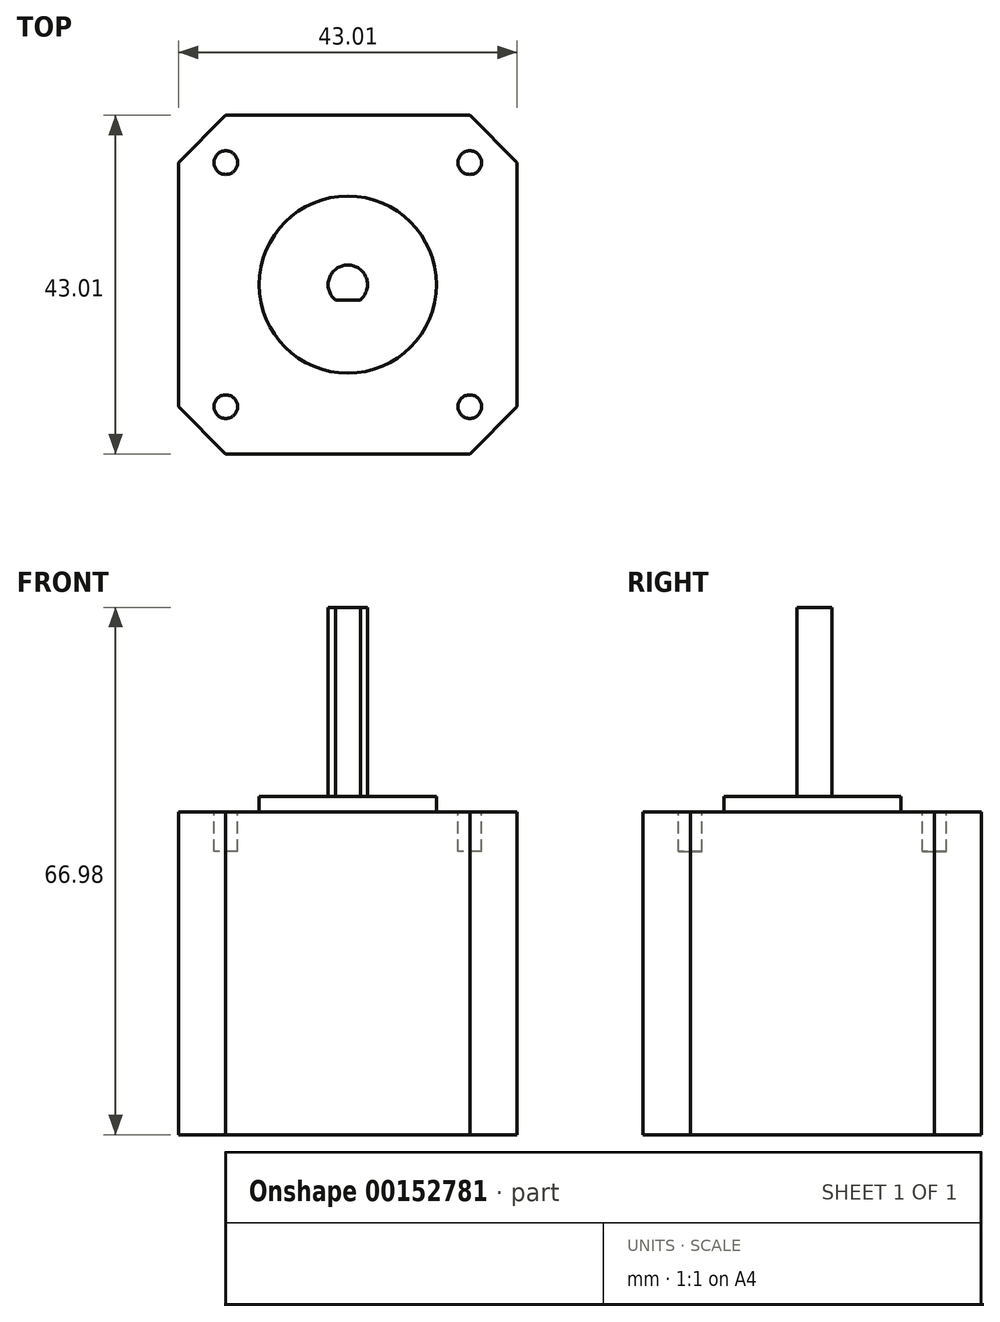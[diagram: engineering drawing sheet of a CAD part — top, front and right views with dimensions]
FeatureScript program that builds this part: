
annotation { "Feature Type Name" : "Feature", "Feature Type Description" : "" }
export const myFeature = defineFeature(function(context is Context, id is Id, definition is map)
    precondition{}
    {
        {
            var Q0;
            Q0=qCreatedBy(makeId("Top.planeOp"),FACE);
            var sketch = newSketch(context, id + "F0", { "sketchPlane" : qUnion([Q0])});
            skLineSegment(sketch, "E0.bottom", {"start": v(0, 0) * mm, "end": v(43, 0) * mm});
            skLineSegment(sketch, "E0.top", {"start": v(0, 43) * mm, "end": v(43, 43) * mm});
            skLineSegment(sketch, "E0.left", {"start": v(0, 0) * mm, "end": v(0, 43) * mm});
            skLineSegment(sketch, "E0.right", {"start": v(43, 0) * mm, "end": v(43, 43) * mm});
            skSolve(sketch);
        }
        {
            var Q0;
            Q0=makeQuery(id+"F0.imprint","IMPRINT",FACE,{"disambiguationData":[TD([[makeQuery(id+"F0.imprint","IMPRINT",EDGE,{"derivedFrom":sQuery(id+"F0.wireOp",EDGE,"E0.bottom")}),1.0]])]});
            extrude(context, id + "F1", {"entities" : qUnion([Q0]), "depth" : 40.98 * mm});
        }
        {
            var Q0;
            Q0=makeQuery(id+"F1.opExtrude","CAP_FACE",FACE,{"disambiguationData":[OSD([sQuery(id+"F0.wireOp",EDGE,"E0.bottom"),sQuery(id+"F0.wireOp",EDGE,"E0.top"),sQuery(id+"F0.wireOp",EDGE,"E0.left"),sQuery(id+"F0.wireOp",EDGE,"E0.right")])],"isStart":false});
            var sketch = newSketch(context, id + "F2", { "sketchPlane" : qUnion([Q0])});
            skLineSegment(sketch, "E1", {"start": v(21.5, 0) * mm, "end": v(21.5, 43) * mm});
            skCircle(sketch, "E2", {"center": v(21.5, 21.5) * mm, "radius": 11.25 * mm});
            skSolve(sketch);
        }
        {
            var Q0;
            Q0=qSketchRegion(id+"F2",true);
            extrude(context, id + "F3", {"entities" : qUnion([Q0]), "operationType" : NewBodyOperationType.ADD, "depth" : 2 * mm});
        }
        {
            var Q0;
            Q0=makeQuery(id+"F1.opExtrude","CAP_FACE",FACE,{"disambiguationData":[OSD([sQuery(id+"F0.wireOp",EDGE,"E0.bottom"),sQuery(id+"F0.wireOp",EDGE,"E0.top"),sQuery(id+"F0.wireOp",EDGE,"E0.left"),sQuery(id+"F0.wireOp",EDGE,"E0.right")])],"isStart":false});
            var sketch = newSketch(context, id + "F4", { "sketchPlane" : qUnion([Q0])});
            skLineSegment(sketch, "E3", {"start": v(6, 21.5) * mm, "end": v(37, 21.5) * mm, "construction": true});
            skLineSegment(sketch, "E4", {"start": v(37, 37) * mm, "end": v(37, 6) * mm, "construction": true});
            skLineSegment(sketch, "E5", {"start": v(6, 37) * mm, "end": v(6, 6) * mm, "construction": true});
            skPoint(sketch, "E6", {"position": v(21.5, 21.5) * mm});
            skCircle(sketch, "E7", {"center": v(6, 6) * mm, "radius": 1.5 * mm});
            skCircle(sketch, "E8", {"center": v(37, 6) * mm, "radius": 1.5 * mm});
            skCircle(sketch, "E9", {"center": v(37, 37) * mm, "radius": 1.5 * mm});
            skCircle(sketch, "E10", {"center": v(6, 37) * mm, "radius": 1.5 * mm});
            skLineSegment(sketch, "E11", {"start": v(21.5, 21.5) * mm, "end": v(21.5, 0) * mm, "construction": true});
            skSolve(sketch);
        }
        {
            var Q0;
            {var subQ0=sQuery(id+"F4.wireOp",EDGE,"E9");var subQ2=sQuery(id+"F4.wireOp",EDGE,"E8");var subQ3=sQuery(id+"F4.wireOp",EDGE,"E10");var subQ5=sQuery(id+"F4.wireOp",EDGE,"E7");Q0=qUnion([makeQuery(id+"F4.imprint","IMPRINT",FACE,{"disambiguationData":[TD([[makeQuery(id+"F4.imprint","IMPRINT",EDGE,{"derivedFrom":subQ0}),1.0]])]}),makeQuery(id+"F4.imprint","IMPRINT",FACE,{"disambiguationData":[TD([[makeQuery(id+"F4.imprint","IMPRINT",EDGE,{"derivedFrom":subQ2}),1.0]])]}),makeQuery(id+"F4.imprint","IMPRINT",FACE,{"disambiguationData":[TD([[makeQuery(id+"F4.imprint","IMPRINT",EDGE,{"derivedFrom":subQ3}),1.0]])]}),makeQuery(id+"F4.imprint","IMPRINT",FACE,{"disambiguationData":[TD([[makeQuery(id+"F4.imprint","IMPRINT",EDGE,{"derivedFrom":subQ5}),1.0]])]})]);}
            extrude(context, id + "F5", {"entities" : qUnion([Q0]), "operationType" : NewBodyOperationType.REMOVE, "oppositeDirection" : true, "depth" : 5 * mm});
        }
        {
            var Q0;
            Q0=makeQuery(id+"F3.opExtrude","CAP_FACE",FACE,{"disambiguationData":[OSD([sQuery(id+"F2.wireOp",EDGE,"E2")])],"isStart":false});
            var sketch = newSketch(context, id + "F6", { "sketchPlane" : qUnion([Q0])});
            skArc(sketch, "E12", {"start": v(23.1, 19.57) * mm, "mid": v(21.5, 24) * mm, "end": v(19.92, 19.57) * mm});
            skLineSegment(sketch, "E13", {"start": v(19.92, 19.57) * mm, "end": v(23.1, 19.57) * mm});
            skLineSegment(sketch, "E14", {"start": v(21.5, 19.57) * mm, "end": v(21.5, 21.5) * mm, "construction": true});
            skSolve(sketch);
        }
        {
            var Q0;
            Q0=qSketchRegion(id+"F6",true);
            extrude(context, id + "F7", {"entities" : qUnion([Q0]), "operationType" : NewBodyOperationType.ADD, "depth" : 24 * mm});
        }
        {
            var Q0;
            Q0=makeQuery(id+"F1.opExtrude","SWEPT_EDGE",EDGE,{"disambiguationData":[OSD([sQuery(id+"F0.wireOp",EDGE,"E0.bottom"),sQuery(id+"F0.wireOp",EDGE,"E0.left")])]});
            var Q1;
            Q1=makeQuery(id+"F1.opExtrude","SWEPT_EDGE",EDGE,{"disambiguationData":[OSD([sQuery(id+"F0.wireOp",EDGE,"E0.top"),sQuery(id+"F0.wireOp",EDGE,"E0.left")])]});
            var Q2;
            Q2=makeQuery(id+"F1.opExtrude","SWEPT_EDGE",EDGE,{"disambiguationData":[OSD([sQuery(id+"F0.wireOp",EDGE,"E0.bottom"),sQuery(id+"F0.wireOp",EDGE,"E0.right")])]});
            var Q3;
            Q3=makeQuery(id+"F1.opExtrude","SWEPT_EDGE",EDGE,{"disambiguationData":[OSD([sQuery(id+"F0.wireOp",EDGE,"E0.top"),sQuery(id+"F0.wireOp",EDGE,"E0.right")])]});
            chamfer(context, id + "F8", {"entities" : qUnion([Q0, Q1, Q2, Q3]), "width" : 6 * mm, "tangentPropagation" : true});
        }
    });
